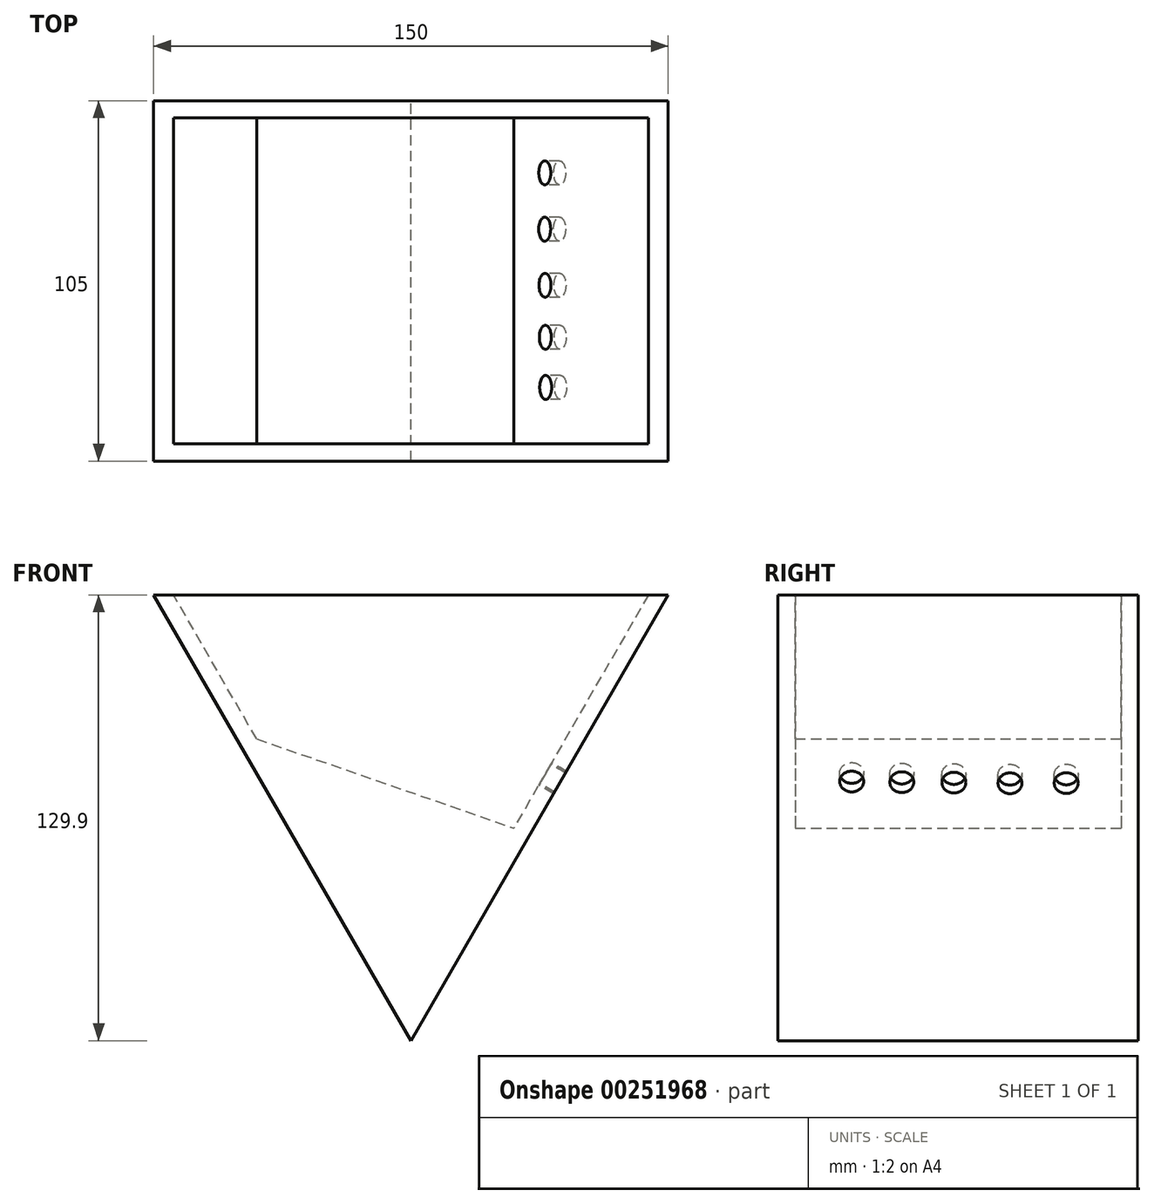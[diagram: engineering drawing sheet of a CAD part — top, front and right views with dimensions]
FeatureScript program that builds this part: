
annotation { "Feature Type Name" : "Feature", "Feature Type Description" : "" }
export const myFeature = defineFeature(function(context is Context, id is Id, definition is map)
    precondition{}
    {
        {
            var Q0;
            Q0=qCreatedBy(makeId("Front.planeOp"),FACE);
            var sketch = newSketch(context, id + "F0", { "sketchPlane" : qUnion([Q0])});
            skLineSegment(sketch, "E0", {"start": v(-75.43, 75.52) * mm, "end": v(74.57, 75.52) * mm});
            skLineSegment(sketch, "E1", {"start": v(74.57, 75.52) * mm, "end": v(-0.43, -54.38) * mm});
            skLineSegment(sketch, "E2", {"start": v(-0.43, -54.38) * mm, "end": v(-75.43, 75.52) * mm});
            skSolve(sketch);
        }
        {
            var Q0;
            Q0=makeQuery(id+"F0.imprint","IMPRINT",FACE,{"disambiguationData":[TD([[makeQuery(id+"F0.imprint","IMPRINT",EDGE,{"derivedFrom":sQuery(id+"F0.wireOp",EDGE,"E0")}),-1.0]])]});
            extrude(context, id + "F1", {"entities" : qUnion([Q0]), "depth" : 105 * mm});
        }
        {
            var Q0;
            Q0=makeQuery(id+"F1.opExtrude","SWEPT_FACE",FACE,{"disambiguationData":[OSD([sQuery(id+"F0.wireOp",EDGE,"E0")])]});
            shell(context, id + "F2", {"entities" : qUnion([Q0]), "thickness" : 5 * mm});
        }
        {
            var Q0;
            {var subQ0=sQuery(id+"F0.wireOp",EDGE,"E2");var subQ1=sQuery(id+"F0.wireOp",EDGE,"E1");var subQ2=sQuery(id+"F0.wireOp",EDGE,"E0");Q0=makeQuery(id+"F2.opShell","OFFSET_FACE",FACE,{"disambiguationData":[OSD([subQ2,subQ1,subQ0]),TDD([makeQuery(id+"F1.opExtrude","CAP_FACE",FACE,{"disambiguationData":[OSD([subQ2,subQ1,subQ0])],"isStart":true})])]});}
            var sketch = newSketch(context, id + "F3", { "sketchPlane" : qUnion([Q0])});
            skLineSegment(sketch, "E3", {"start": v(-45.43, 33.56) * mm, "end": v(29.57, 7.58) * mm});
            skLineSegment(sketch, "E4", {"start": v(29.57, 7.58) * mm, "end": v(-0.43, -44.38) * mm});
            skLineSegment(sketch, "E5", {"start": v(-0.43, -44.38) * mm, "end": v(-45.43, 33.56) * mm});
            skSolve(sketch);
        }
        {
            var Q0;
            Q0=makeQuery(id+"F3.imprint","IMPRINT",FACE,{"disambiguationData":[TD([[makeQuery(id+"F3.imprint","IMPRINT",EDGE,{"derivedFrom":sQuery(id+"F3.wireOp",EDGE,"E3")}),-1.0]])]});
            extrude(context, id + "F4", {"entities" : qUnion([Q0]), "operationType" : NewBodyOperationType.ADD, "depth" : 95 * mm});
        }
        {
            var Q0;
            Q0=makeQuery(id+"F2.opShell","OFFSET_FACE",FACE,{"disambiguationData":[OSD([sQuery(id+"F0.wireOp",EDGE,"E1")])]});
            var sketch = newSketch(context, id + "F5", { "sketchPlane" : qUnion([Q0])});
            skCircle(sketch, "E6", {"center": v(37.38, 39.31) * mm, "radius": 5 * mm});
            skCircle(sketch, "E7", {"center": v(53.74, 39.53) * mm, "radius": 5 * mm});
            skCircle(sketch, "E8", {"center": v(68.92, 39.67) * mm, "radius": 5 * mm});
            skCircle(sketch, "E9", {"center": v(83.52, 39.9) * mm, "radius": 5 * mm});
            skCircle(sketch, "E10", {"center": v(20.98, 39.37) * mm, "radius": 5 * mm});
            skSolve(sketch);
        }
        {
            var Q0;
            Q0=sQuery(id+"F5.wireOp",VERTEX,"E9.center");
            var Q1;
            Q1=sQuery(id+"F5.wireOp",VERTEX,"E10.center");
            var Q2;
            Q2=sQuery(id+"F5.wireOp",VERTEX,"E6.center");
            var Q3;
            Q3=sQuery(id+"F5.wireOp",VERTEX,"E7.center");
            var Q4;
            Q4=sQuery(id+"F5.wireOp",VERTEX,"E8.center");
            var Q5;
            Q5=makeQuery(id+"F1.opExtrude","SWEPT_BODY",BODY,{"disambiguationData":[OSD([sQuery(id+"F0.wireOp",EDGE,"E0"),sQuery(id+"F0.wireOp",EDGE,"E1"),sQuery(id+"F0.wireOp",EDGE,"E2")])]});
            hole(context, id + "F6", {"style" : HoleStyle.SIMPLE, "endStyle" : HoleEndStyle.THROUGH, "holeDiameter" : 7 * mm, "tappedDepth" : 12 * mm, "tapClearance" : 3, "locations" : qUnion([Q0, Q1, Q2, Q3, Q4]), "scope" : qUnion([Q5])});
        }
    });
